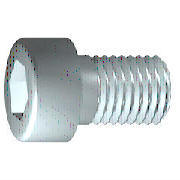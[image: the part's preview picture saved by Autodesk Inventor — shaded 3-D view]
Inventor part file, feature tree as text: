
AUTODESK INVENTOR PART (.ipt)
format: ipt  version: 2022.1 (Build 261234000, 234)  size: 188,416 bytes
history: native  units: mm (DEFAULTED — no unit token found)
features: sketch x2, other x1, extrude x1, plane x1, fillet x1
ambient origin geometry x7: Origin, YZ Plane, XY Plane, X Axis, Y Axis, Z Axis, Center Point
bodies: Solid1 (feature_tree)
feature tree (6):
  other  "Cuerpo"
  extrude  "Ranura"  Depth=10.0mm
  plane  "Work Plane1"
  fillet  "Fillet2"  Radius=10.0mm
  sketch  "Boceto1"  dims[d1=32.0mm d2=0.920275mm d3=10.0mm]
  sketch  "Boceto2"  dims[d4=5.0mm d5=60.0deg d6=10.0mm d7=10.0mm d8=9.237604mm d9=16.0mm d10=90.0deg d11=10.0mm d12=0.0mm d13=32.0mm d14=0.0mm d15=0.920175mm d16=0.920175mm d17=1.0mm d19=0.0mm d26=65.0mm d27=45.0deg d28=0.0mm d29=0.0mm d30=0.1mm]
